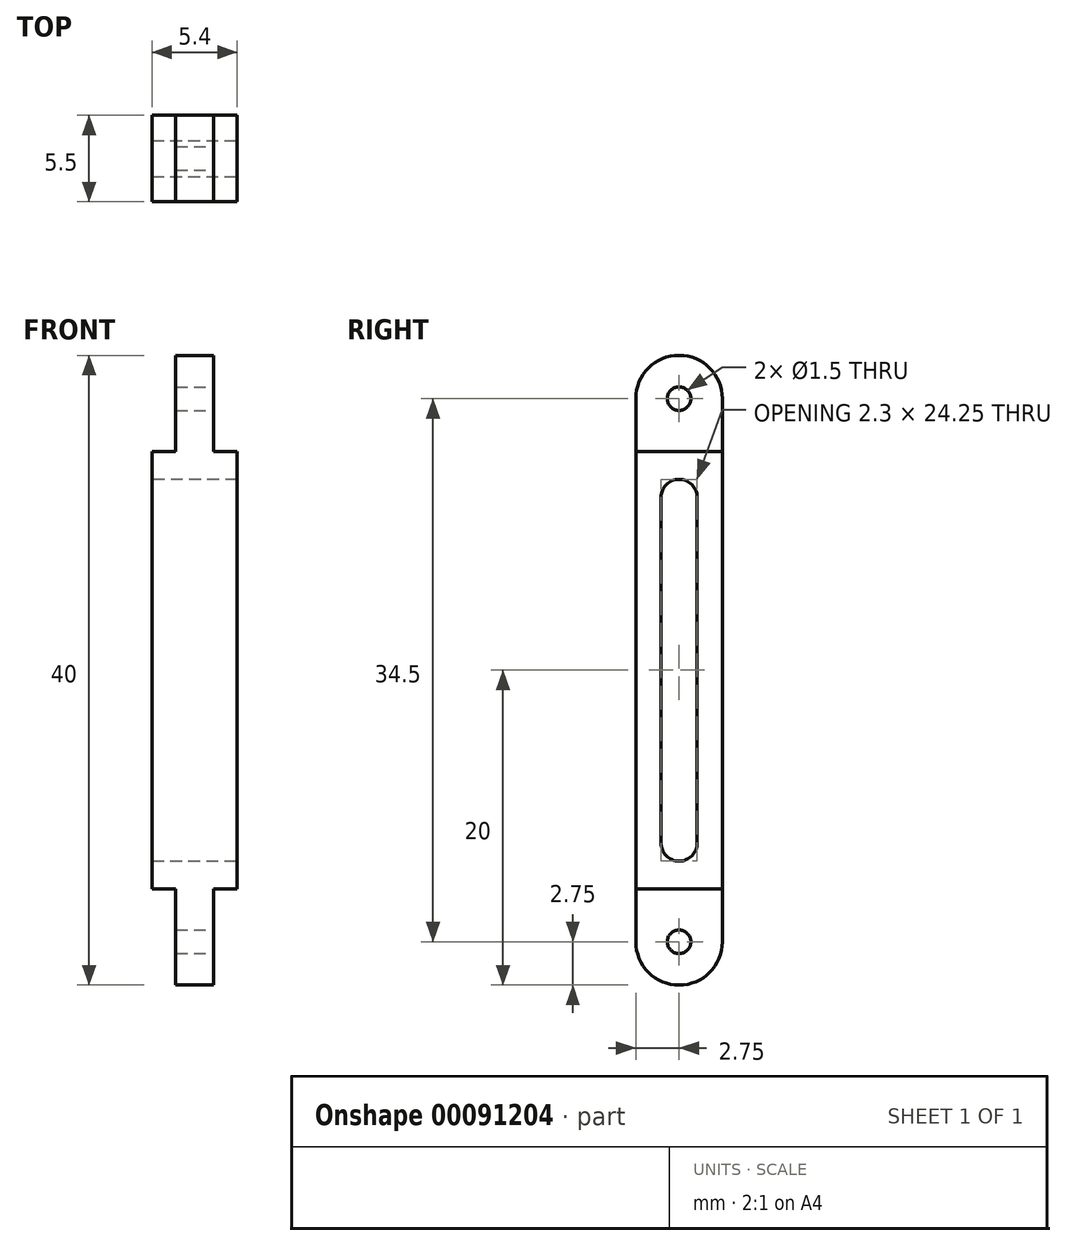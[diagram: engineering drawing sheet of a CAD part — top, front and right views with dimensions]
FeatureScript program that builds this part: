
annotation { "Feature Type Name" : "Feature", "Feature Type Description" : "" }
export const myFeature = defineFeature(function(context is Context, id is Id, definition is map)
    precondition{}
    {
        {
            var Q0;
            Q0=qCreatedBy(makeId("Front.planeOp"),FACE);
            var sketch = newSketch(context, id + "F0", { "sketchPlane" : qUnion([Q0])});
            skLineSegment(sketch, "E0.bottom", {"start": v(-2.7, 20) * mm, "end": v(2.7, 20) * mm});
            skLineSegment(sketch, "E0.top", {"start": v(-2.7, -20) * mm, "end": v(2.7, -20) * mm});
            skLineSegment(sketch, "E0.left", {"start": v(-2.7, 20) * mm, "end": v(-2.7, -20) * mm});
            skLineSegment(sketch, "E0.right", {"start": v(2.7, 20) * mm, "end": v(2.7, -20) * mm});
            skPoint(sketch, "E0.middle", {"position": v(0, 0) * mm});
            skSolve(sketch);
        }
        {
            var Q0;
            Q0 = qSketchRegion(id + "F0", true);
            extrude(context, id + "F1", {"entities" : qUnion([Q0]), "depth" : 5.5 * mm});
        }
        {
            var Q0;
            Q0=makeQuery(id+"F1.opExtrude","CAP_FACE",FACE,{"disambiguationData":[OSD([sQuery(id+"F0.wireOp",EDGE,"E0.bottom"),sQuery(id+"F0.wireOp",EDGE,"E0.top"),sQuery(id+"F0.wireOp",EDGE,"E0.left"),sQuery(id+"F0.wireOp",EDGE,"E0.right")])],"isStart":false});
            var sketch = newSketch(context, id + "F2", { "sketchPlane" : qUnion([Q0])});
            skLineSegment(sketch, "E1.bottom", {"start": v(-2.7, 20) * mm, "end": v(-1.2, 20) * mm});
            skLineSegment(sketch, "E1.top", {"start": v(-2.7, 13.9) * mm, "end": v(-1.2, 13.9) * mm});
            skLineSegment(sketch, "E1.left", {"start": v(-2.7, 20) * mm, "end": v(-2.7, 13.9) * mm});
            skLineSegment(sketch, "E1.right", {"start": v(-1.2, 20) * mm, "end": v(-1.2, 13.9) * mm});
            skSolve(sketch);
        }
        {
            var Q0;
            Q0 = qSketchRegion(id + "F2", true);
            extrude(context, id + "F3", {"entities" : qUnion([Q0]), "operationType" : NewBodyOperationType.REMOVE, "endBound" : BoundingType.THROUGH_ALL, "oppositeDirection" : true, "depth" : 25 * mm});
        }
        {
            var Q0;
            Q0=makeQuery(id+"F1.opExtrude","CAP_FACE",FACE,{"disambiguationData":[OSD([sQuery(id+"F0.wireOp",EDGE,"E0.bottom"),sQuery(id+"F0.wireOp",EDGE,"E0.top"),sQuery(id+"F0.wireOp",EDGE,"E0.left"),sQuery(id+"F0.wireOp",EDGE,"E0.right")])],"isStart":false});
            var sketch = newSketch(context, id + "F4", { "sketchPlane" : qUnion([Q0])});
            skLineSegment(sketch, "E2.bottom", {"start": v(2.7, 20) * mm, "end": v(1.2, 20) * mm});
            skLineSegment(sketch, "E2.top", {"start": v(2.7, 13.9) * mm, "end": v(1.2, 13.9) * mm});
            skLineSegment(sketch, "E2.left", {"start": v(2.7, 20) * mm, "end": v(2.7, 13.9) * mm});
            skLineSegment(sketch, "E2.right", {"start": v(1.2, 20) * mm, "end": v(1.2, 13.9) * mm});
            skSolve(sketch);
        }
        {
            var Q0;
            Q0 = qSketchRegion(id + "F4", true);
            extrude(context, id + "F5", {"entities" : qUnion([Q0]), "operationType" : NewBodyOperationType.REMOVE, "oppositeDirection" : true, "depth" : 25 * mm});
        }
        {
            var Q0;
            Q0=makeQuery(id+"F1.opExtrude","CAP_FACE",FACE,{"disambiguationData":[OSD([sQuery(id+"F0.wireOp",EDGE,"E0.bottom"),sQuery(id+"F0.wireOp",EDGE,"E0.top"),sQuery(id+"F0.wireOp",EDGE,"E0.left"),sQuery(id+"F0.wireOp",EDGE,"E0.right")])],"isStart":false});
            var sketch = newSketch(context, id + "F6", { "sketchPlane" : qUnion([Q0])});
            skLineSegment(sketch, "E3.bottom", {"start": v(-2.7, -20) * mm, "end": v(-1.2, -20) * mm});
            skLineSegment(sketch, "E3.top", {"start": v(-2.7, -13.9) * mm, "end": v(-1.2, -13.9) * mm});
            skLineSegment(sketch, "E3.left", {"start": v(-2.7, -20) * mm, "end": v(-2.7, -13.9) * mm});
            skLineSegment(sketch, "E3.right", {"start": v(-1.2, -20) * mm, "end": v(-1.2, -13.9) * mm});
            skSolve(sketch);
        }
        {
            var Q0;
            Q0 = qSketchRegion(id + "F6", true);
            extrude(context, id + "F7", {"entities" : qUnion([Q0]), "operationType" : NewBodyOperationType.REMOVE, "endBound" : BoundingType.THROUGH_ALL, "oppositeDirection" : true, "depth" : 25 * mm});
        }
        {
            var Q0;
            Q0=makeQuery(id+"F1.opExtrude","CAP_FACE",FACE,{"disambiguationData":[OSD([sQuery(id+"F0.wireOp",EDGE,"E0.bottom"),sQuery(id+"F0.wireOp",EDGE,"E0.top"),sQuery(id+"F0.wireOp",EDGE,"E0.left"),sQuery(id+"F0.wireOp",EDGE,"E0.right")])],"isStart":false});
            var sketch = newSketch(context, id + "F8", { "sketchPlane" : qUnion([Q0])});
            skLineSegment(sketch, "E4.bottom", {"start": v(2.7, -20) * mm, "end": v(1.2, -20) * mm});
            skLineSegment(sketch, "E4.top", {"start": v(2.7, -13.9) * mm, "end": v(1.2, -13.9) * mm});
            skLineSegment(sketch, "E4.left", {"start": v(2.7, -20) * mm, "end": v(2.7, -13.9) * mm});
            skLineSegment(sketch, "E4.right", {"start": v(1.2, -20) * mm, "end": v(1.2, -13.9) * mm});
            skSolve(sketch);
        }
        {
            var Q0;
            Q0 = qSketchRegion(id + "F8", true);
            extrude(context, id + "F9", {"entities" : qUnion([Q0]), "operationType" : NewBodyOperationType.REMOVE, "endBound" : BoundingType.THROUGH_ALL, "oppositeDirection" : true, "depth" : 25 * mm});
        }
        {
            var Q0;
            Q0=makeQuery(id+"F1.opExtrude","CAP_EDGE",EDGE,{"disambiguationData":[OSD([sQuery(id+"F0.wireOp",EDGE,"E0.bottom")])],"isStart":false});
            fillet(context, id + "F10", {"entities" : qUnion([Q0]), "radius" : 2.75 * mm, "tangentPropagation" : true, "allowEdgeOverflow" : false});
        }
        {
            var Q0;
            Q0=makeQuery(id+"F1.opExtrude","CAP_EDGE",EDGE,{"disambiguationData":[OSD([sQuery(id+"F0.wireOp",EDGE,"E0.bottom")])],"isStart":true});
            fillet(context, id + "F11", {"entities" : qUnion([Q0]), "radius" : 2.75 * mm, "tangentPropagation" : true, "allowEdgeOverflow" : false});
        }
        {
            var Q0;
            Q0=makeQuery(id+"F1.opExtrude","CAP_EDGE",EDGE,{"disambiguationData":[OSD([sQuery(id+"F0.wireOp",EDGE,"E0.top")])],"isStart":true});
            fillet(context, id + "F12", {"entities" : qUnion([Q0]), "radius" : 2.75 * mm, "tangentPropagation" : true, "allowEdgeOverflow" : false});
        }
        {
            var Q0;
            Q0=makeQuery(id+"F1.opExtrude","CAP_EDGE",EDGE,{"disambiguationData":[OSD([sQuery(id+"F0.wireOp",EDGE,"E0.top")])],"isStart":false});
            fillet(context, id + "F13", {"entities" : qUnion([Q0]), "radius" : 2.75 * mm, "tangentPropagation" : true, "allowEdgeOverflow" : false});
        }
        {
            var Q0;
            Q0=qCreatedBy(makeId("Right.planeOp"),FACE);
            var sketch = newSketch(context, id + "F14", { "sketchPlane" : qUnion([Q0])});
            skLineSegment(sketch, "E5.bottom", {"start": v(-1.6, 12.13) * mm, "end": v(-3.9, 12.13) * mm});
            skLineSegment(sketch, "E5.top", {"start": v(-1.6, -12.12) * mm, "end": v(-3.9, -12.12) * mm});
            skLineSegment(sketch, "E5.left", {"start": v(-1.6, 12.12) * mm, "end": v(-1.6, -12.12) * mm});
            skLineSegment(sketch, "E5.right", {"start": v(-3.9, 12.13) * mm, "end": v(-3.9, -12.12) * mm});
            skPoint(sketch, "E5.middle", {"position": v(-2.75, 0) * mm});
            skSolve(sketch);
        }
        {
            var Q0;
            Q0 = qSketchRegion(id + "F14", true);
            extrude(context, id + "F15", {"entities" : qUnion([Q0]), "operationType" : NewBodyOperationType.REMOVE, "endBound" : BoundingType.THROUGH_ALL, "oppositeDirection" : true, "depth" : 25 * mm});
        }
        {
            var Q0;
            Q0=makeQuery(id+"F14.imprint","IMPRINT",FACE,{"disambiguationData":[TD([[makeQuery(id+"F14.imprint","IMPRINT",EDGE,{"derivedFrom":sQuery(id+"F14.wireOp",EDGE,"E5.bottom")}),1.0]])]});
            extrude(context, id + "F16", {"entities" : qUnion([Q0]), "operationType" : NewBodyOperationType.REMOVE, "endBound" : BoundingType.THROUGH_ALL, "depth" : 25 * mm});
        }
        {
            var Q0;
            {var subQ0=sQuery(id+"F14.wireOp",EDGE,"E5.right");var subQ1=sQuery(id+"F14.wireOp",EDGE,"E5.bottom");Q0=makeQuery(id+"F16.boolean.opBoolean","MERGE",EDGE,{"derivedFrom":[makeQuery(id+"F15.boolean.opBoolean","COPY",EDGE,{"derivedFrom":makeQuery(id+"F15.opExtrude","SWEPT_EDGE",EDGE,{"disambiguationData":[OSD([subQ1,subQ0])]})}),makeQuery(id+"F16.opExtrude","SWEPT_EDGE",EDGE,{"disambiguationData":[OSD([subQ1,subQ0])]})]});}
            fillet(context, id + "F17", {"entities" : qUnion([Q0]), "radius" : 1.15 * mm, "tangentPropagation" : true, "allowEdgeOverflow" : false});
        }
        {
            var Q0;
            {var subQ0=sQuery(id+"F14.wireOp",EDGE,"E5.left");var subQ1=sQuery(id+"F14.wireOp",EDGE,"E5.bottom");Q0=makeQuery(id+"F16.boolean.opBoolean","MERGE",EDGE,{"derivedFrom":[makeQuery(id+"F15.boolean.opBoolean","COPY",EDGE,{"derivedFrom":makeQuery(id+"F15.opExtrude","SWEPT_EDGE",EDGE,{"disambiguationData":[OSD([subQ1,subQ0])]})}),makeQuery(id+"F16.opExtrude","SWEPT_EDGE",EDGE,{"disambiguationData":[OSD([subQ1,subQ0])]})]});}
            fillet(context, id + "F18", {"entities" : qUnion([Q0]), "radius" : 1.15 * mm, "tangentPropagation" : true, "allowEdgeOverflow" : false});
        }
        {
            var Q0;
            {var subQ0=sQuery(id+"F14.wireOp",EDGE,"E5.right");var subQ1=sQuery(id+"F14.wireOp",EDGE,"E5.top");Q0=makeQuery(id+"F16.boolean.opBoolean","MERGE",EDGE,{"derivedFrom":[makeQuery(id+"F15.boolean.opBoolean","COPY",EDGE,{"derivedFrom":makeQuery(id+"F15.opExtrude","SWEPT_EDGE",EDGE,{"disambiguationData":[OSD([subQ1,subQ0])]})}),makeQuery(id+"F16.opExtrude","SWEPT_EDGE",EDGE,{"disambiguationData":[OSD([subQ1,subQ0])]})]});}
            fillet(context, id + "F19", {"entities" : qUnion([Q0]), "radius" : 1.15 * mm, "tangentPropagation" : true, "allowEdgeOverflow" : false});
        }
        {
            var Q0;
            {var subQ0=sQuery(id+"F14.wireOp",EDGE,"E5.left");var subQ1=sQuery(id+"F14.wireOp",EDGE,"E5.top");Q0=makeQuery(id+"F16.boolean.opBoolean","MERGE",EDGE,{"derivedFrom":[makeQuery(id+"F15.boolean.opBoolean","COPY",EDGE,{"derivedFrom":makeQuery(id+"F15.opExtrude","SWEPT_EDGE",EDGE,{"disambiguationData":[OSD([subQ1,subQ0])]})}),makeQuery(id+"F16.opExtrude","SWEPT_EDGE",EDGE,{"disambiguationData":[OSD([subQ1,subQ0])]})]});}
            fillet(context, id + "F20", {"entities" : qUnion([Q0]), "radius" : 1.15 * mm, "tangentPropagation" : true, "allowEdgeOverflow" : false});
        }
        {
            var Q0;
            Q0=makeQuery(id+"F5.boolean.opBoolean","COPY",FACE,{"derivedFrom":makeQuery(id+"F5.opExtrude","SWEPT_FACE",FACE,{"disambiguationData":[OSD([sQuery(id+"F4.wireOp",EDGE,"E2.right")])]})});
            var sketch = newSketch(context, id + "F21", { "sketchPlane" : qUnion([Q0])});
            skCircle(sketch, "E6", {"center": v(-2.75, 17.25) * mm, "radius": 0.75 * mm});
            skSolve(sketch);
        }
        {
            var Q0;
            Q0 = qSketchRegion(id + "F21", true);
            extrude(context, id + "F22", {"entities" : qUnion([Q0]), "operationType" : NewBodyOperationType.REMOVE, "endBound" : BoundingType.THROUGH_ALL, "oppositeDirection" : true, "depth" : 25 * mm});
        }
        {
            var Q0;
            Q0=makeQuery(id+"F9.boolean.opBoolean","COPY",FACE,{"derivedFrom":makeQuery(id+"F9.opExtrude","SWEPT_FACE",FACE,{"disambiguationData":[OSD([sQuery(id+"F8.wireOp",EDGE,"E4.right")])]})});
            var sketch = newSketch(context, id + "F23", { "sketchPlane" : qUnion([Q0])});
            skCircle(sketch, "E7", {"center": v(-2.75, -17.25) * mm, "radius": 0.75 * mm});
            skSolve(sketch);
        }
        {
            var Q0;
            Q0 = qSketchRegion(id + "F23", true);
            extrude(context, id + "F24", {"entities" : qUnion([Q0]), "operationType" : NewBodyOperationType.REMOVE, "endBound" : BoundingType.THROUGH_ALL, "oppositeDirection" : true, "depth" : 25 * mm});
        }
    });
